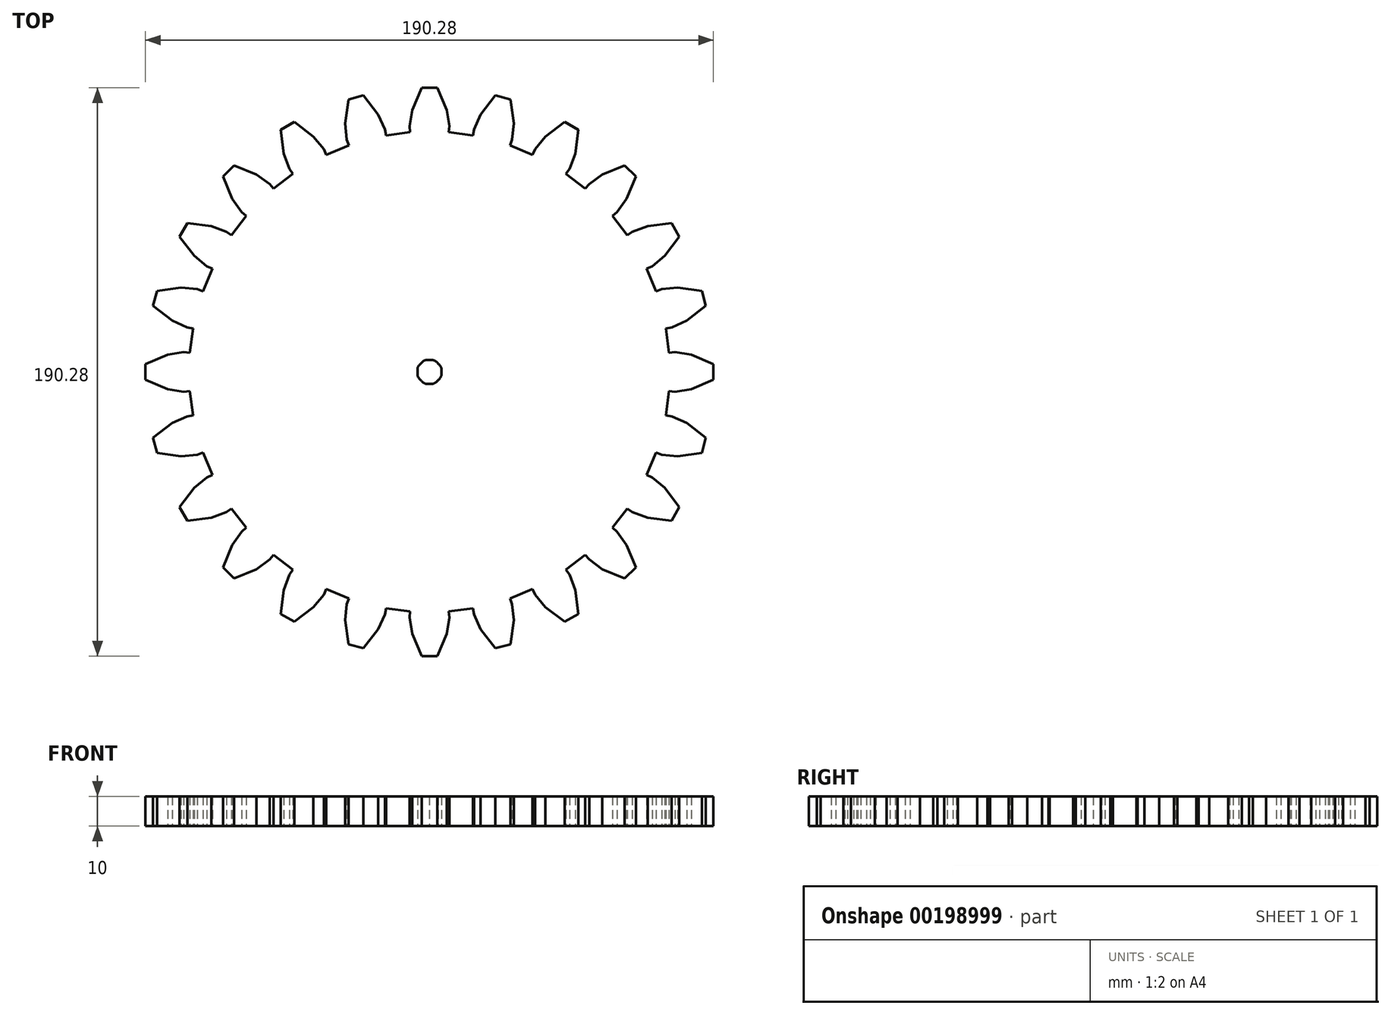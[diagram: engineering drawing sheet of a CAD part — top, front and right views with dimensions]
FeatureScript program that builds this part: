
annotation { "Feature Type Name" : "Feature", "Feature Type Description" : "" }
export const myFeature = defineFeature(function(context is Context, id is Id, definition is map)
    precondition{}
    {
        {
            var Q0;
            Q0=qCreatedBy(makeId("Top.planeOp"),FACE);
            var sketch = newSketch(context, id + "F0", { "sketchPlane" : qUnion([Q0])});
            skFitSpline(sketch, "E0", {"points": [v(4, 0) * mm, v(4, -1.06) * mm, v(3.58, -2.08) * mm, v(2.83, -2.83) * mm]});
            skFitSpline(sketch, "E1", {"points": [v(2.83, -2.83) * mm, v(2.08, -3.58) * mm, v(1.06, -4) * mm, v(0, -4) * mm]});
            skFitSpline(sketch, "E2", {"points": [v(0, -4) * mm, v(-1.06, -4) * mm, v(-2.08, -3.58) * mm, v(-2.83, -2.83) * mm]});
            skFitSpline(sketch, "E3", {"points": [v(-2.83, -2.83) * mm, v(-3.58, -2.08) * mm, v(-4, -1.06) * mm, v(-4, 0) * mm]});
            skFitSpline(sketch, "E4", {"points": [v(-4, 0) * mm, v(-4, 1.06) * mm, v(-3.58, 2.08) * mm, v(-2.83, 2.83) * mm]});
            skFitSpline(sketch, "E5", {"points": [v(-2.83, 2.83) * mm, v(-2.08, 3.58) * mm, v(-1.06, 4) * mm, v(0, 4) * mm]});
            skFitSpline(sketch, "E6", {"points": [v(0, 4) * mm, v(1.06, 4) * mm, v(2.08, 3.58) * mm, v(2.83, 2.83) * mm]});
            skFitSpline(sketch, "E7", {"points": [v(2.83, 2.83) * mm, v(3.58, 2.08) * mm, v(4, 1.06) * mm, v(4, 0) * mm]});
            skLineSegment(sketch, "E8", {"start": v(80.27, 6.46) * mm, "end": v(82.29, 6.63) * mm});
            skLineSegment(sketch, "E9", {"start": v(82.29, 6.63) * mm, "end": v(87.67, 5.75) * mm});
            skLineSegment(sketch, "E10", {"start": v(87.67, 5.75) * mm, "end": v(95.14, 2.62) * mm});
            skLineSegment(sketch, "E11", {"start": v(95.14, 2.62) * mm, "end": v(95.14, -2.62) * mm});
            skLineSegment(sketch, "E12", {"start": v(95.14, -2.62) * mm, "end": v(87.67, -5.75) * mm});
            skLineSegment(sketch, "E13", {"start": v(87.67, -5.75) * mm, "end": v(82.29, -6.63) * mm});
            skLineSegment(sketch, "E14", {"start": v(82.29, -6.63) * mm, "end": v(80.27, -6.46) * mm});
            skLineSegment(sketch, "E15", {"start": v(80.27, -6.46) * mm, "end": v(79.21, -14.53) * mm});
            skLineSegment(sketch, "E16", {"start": v(79.21, -14.53) * mm, "end": v(81.2, -14.9) * mm});
            skLineSegment(sketch, "E17", {"start": v(81.2, -14.9) * mm, "end": v(86.17, -17.14) * mm});
            skLineSegment(sketch, "E18", {"start": v(86.17, -17.14) * mm, "end": v(92.57, -22.1) * mm});
            skLineSegment(sketch, "E19", {"start": v(92.57, -22.1) * mm, "end": v(91.22, -27.15) * mm});
            skLineSegment(sketch, "E20", {"start": v(91.22, -27.15) * mm, "end": v(83.2, -28.24) * mm});
            skLineSegment(sketch, "E21", {"start": v(83.2, -28.24) * mm, "end": v(77.77, -27.7) * mm});
            skLineSegment(sketch, "E22", {"start": v(77.77, -27.7) * mm, "end": v(75.86, -27.02) * mm});
            skLineSegment(sketch, "E23", {"start": v(75.86, -27.02) * mm, "end": v(72.75, -34.54) * mm});
            skLineSegment(sketch, "E24", {"start": v(72.75, -34.54) * mm, "end": v(74.58, -35.4) * mm});
            skLineSegment(sketch, "E25", {"start": v(74.58, -35.4) * mm, "end": v(78.8, -38.86) * mm});
            skLineSegment(sketch, "E26", {"start": v(78.8, -38.86) * mm, "end": v(83.7, -45.3) * mm});
            skLineSegment(sketch, "E27", {"start": v(83.7, -45.3) * mm, "end": v(81.08, -49.84) * mm});
            skLineSegment(sketch, "E28", {"start": v(81.08, -49.84) * mm, "end": v(73.05, -48.8) * mm});
            skLineSegment(sketch, "E29", {"start": v(73.05, -48.8) * mm, "end": v(67.95, -46.88) * mm});
            skLineSegment(sketch, "E30", {"start": v(67.95, -46.88) * mm, "end": v(66.29, -45.73) * mm});
            skLineSegment(sketch, "E31", {"start": v(66.29, -45.73) * mm, "end": v(61.33, -52.2) * mm});
            skLineSegment(sketch, "E32", {"start": v(61.33, -52.2) * mm, "end": v(62.87, -53.5) * mm});
            skLineSegment(sketch, "E33", {"start": v(62.87, -53.5) * mm, "end": v(66.05, -57.93) * mm});
            skLineSegment(sketch, "E34", {"start": v(66.05, -57.93) * mm, "end": v(69.13, -65.42) * mm});
            skLineSegment(sketch, "E35", {"start": v(69.13, -65.42) * mm, "end": v(65.42, -69.13) * mm});
            skLineSegment(sketch, "E36", {"start": v(65.42, -69.13) * mm, "end": v(57.93, -66.05) * mm});
            skLineSegment(sketch, "E37", {"start": v(57.93, -66.05) * mm, "end": v(53.5, -62.87) * mm});
            skLineSegment(sketch, "E38", {"start": v(53.5, -62.87) * mm, "end": v(52.2, -61.33) * mm});
            skLineSegment(sketch, "E39", {"start": v(52.2, -61.33) * mm, "end": v(45.73, -66.29) * mm});
            skLineSegment(sketch, "E40", {"start": v(45.73, -66.29) * mm, "end": v(46.88, -67.95) * mm});
            skLineSegment(sketch, "E41", {"start": v(46.88, -67.95) * mm, "end": v(48.8, -73.05) * mm});
            skLineSegment(sketch, "E42", {"start": v(48.8, -73.05) * mm, "end": v(49.84, -81.08) * mm});
            skLineSegment(sketch, "E43", {"start": v(49.84, -81.08) * mm, "end": v(45.3, -83.7) * mm});
            skLineSegment(sketch, "E44", {"start": v(45.3, -83.7) * mm, "end": v(38.86, -78.8) * mm});
            skLineSegment(sketch, "E45", {"start": v(38.86, -78.8) * mm, "end": v(35.4, -74.58) * mm});
            skLineSegment(sketch, "E46", {"start": v(35.4, -74.58) * mm, "end": v(34.54, -72.75) * mm});
            skLineSegment(sketch, "E47", {"start": v(34.54, -72.75) * mm, "end": v(27.02, -75.86) * mm});
            skLineSegment(sketch, "E48", {"start": v(27.02, -75.86) * mm, "end": v(27.7, -77.77) * mm});
            skLineSegment(sketch, "E49", {"start": v(27.7, -77.77) * mm, "end": v(28.24, -83.2) * mm});
            skLineSegment(sketch, "E50", {"start": v(28.24, -83.2) * mm, "end": v(27.15, -91.22) * mm});
            skLineSegment(sketch, "E51", {"start": v(27.15, -91.22) * mm, "end": v(22.1, -92.57) * mm});
            skLineSegment(sketch, "E52", {"start": v(22.1, -92.57) * mm, "end": v(17.14, -86.17) * mm});
            skLineSegment(sketch, "E53", {"start": v(17.14, -86.17) * mm, "end": v(14.9, -81.2) * mm});
            skLineSegment(sketch, "E54", {"start": v(14.9, -81.2) * mm, "end": v(14.53, -79.21) * mm});
            skLineSegment(sketch, "E55", {"start": v(14.53, -79.21) * mm, "end": v(6.46, -80.27) * mm});
            skLineSegment(sketch, "E56", {"start": v(6.46, -80.27) * mm, "end": v(6.63, -82.29) * mm});
            skLineSegment(sketch, "E57", {"start": v(6.63, -82.29) * mm, "end": v(5.75, -87.67) * mm});
            skLineSegment(sketch, "E58", {"start": v(5.75, -87.67) * mm, "end": v(2.62, -95.14) * mm});
            skLineSegment(sketch, "E59", {"start": v(2.62, -95.14) * mm, "end": v(-2.62, -95.14) * mm});
            skLineSegment(sketch, "E60", {"start": v(-2.62, -95.14) * mm, "end": v(-5.75, -87.67) * mm});
            skLineSegment(sketch, "E61", {"start": v(-5.75, -87.67) * mm, "end": v(-6.63, -82.29) * mm});
            skLineSegment(sketch, "E62", {"start": v(-6.63, -82.29) * mm, "end": v(-6.46, -80.27) * mm});
            skLineSegment(sketch, "E63", {"start": v(-6.46, -80.27) * mm, "end": v(-14.53, -79.21) * mm});
            skLineSegment(sketch, "E64", {"start": v(-14.53, -79.21) * mm, "end": v(-14.9, -81.2) * mm});
            skLineSegment(sketch, "E65", {"start": v(-14.9, -81.2) * mm, "end": v(-17.14, -86.17) * mm});
            skLineSegment(sketch, "E66", {"start": v(-17.14, -86.17) * mm, "end": v(-22.1, -92.57) * mm});
            skLineSegment(sketch, "E67", {"start": v(-22.1, -92.57) * mm, "end": v(-27.15, -91.22) * mm});
            skLineSegment(sketch, "E68", {"start": v(-27.15, -91.22) * mm, "end": v(-28.24, -83.2) * mm});
            skLineSegment(sketch, "E69", {"start": v(-28.24, -83.2) * mm, "end": v(-27.7, -77.77) * mm});
            skLineSegment(sketch, "E70", {"start": v(-27.7, -77.77) * mm, "end": v(-27.02, -75.86) * mm});
            skLineSegment(sketch, "E71", {"start": v(-27.02, -75.86) * mm, "end": v(-34.54, -72.75) * mm});
            skLineSegment(sketch, "E72", {"start": v(-34.54, -72.75) * mm, "end": v(-35.4, -74.58) * mm});
            skLineSegment(sketch, "E73", {"start": v(-35.4, -74.58) * mm, "end": v(-38.86, -78.8) * mm});
            skLineSegment(sketch, "E74", {"start": v(-38.86, -78.8) * mm, "end": v(-45.3, -83.7) * mm});
            skLineSegment(sketch, "E75", {"start": v(-45.3, -83.7) * mm, "end": v(-49.84, -81.08) * mm});
            skLineSegment(sketch, "E76", {"start": v(-49.84, -81.08) * mm, "end": v(-48.8, -73.05) * mm});
            skLineSegment(sketch, "E77", {"start": v(-48.8, -73.05) * mm, "end": v(-46.88, -67.95) * mm});
            skLineSegment(sketch, "E78", {"start": v(-46.88, -67.95) * mm, "end": v(-45.73, -66.29) * mm});
            skLineSegment(sketch, "E79", {"start": v(-45.73, -66.29) * mm, "end": v(-52.2, -61.33) * mm});
            skLineSegment(sketch, "E80", {"start": v(-52.2, -61.33) * mm, "end": v(-53.5, -62.87) * mm});
            skLineSegment(sketch, "E81", {"start": v(-53.5, -62.87) * mm, "end": v(-57.93, -66.05) * mm});
            skLineSegment(sketch, "E82", {"start": v(-57.93, -66.05) * mm, "end": v(-65.42, -69.13) * mm});
            skLineSegment(sketch, "E83", {"start": v(-65.42, -69.13) * mm, "end": v(-69.13, -65.42) * mm});
            skLineSegment(sketch, "E84", {"start": v(-69.13, -65.42) * mm, "end": v(-66.05, -57.93) * mm});
            skLineSegment(sketch, "E85", {"start": v(-66.05, -57.93) * mm, "end": v(-62.87, -53.5) * mm});
            skLineSegment(sketch, "E86", {"start": v(-62.87, -53.5) * mm, "end": v(-61.33, -52.2) * mm});
            skLineSegment(sketch, "E87", {"start": v(-61.33, -52.2) * mm, "end": v(-66.29, -45.73) * mm});
            skLineSegment(sketch, "E88", {"start": v(-66.29, -45.73) * mm, "end": v(-67.95, -46.88) * mm});
            skLineSegment(sketch, "E89", {"start": v(-67.95, -46.88) * mm, "end": v(-73.05, -48.8) * mm});
            skLineSegment(sketch, "E90", {"start": v(-73.05, -48.8) * mm, "end": v(-81.08, -49.84) * mm});
            skLineSegment(sketch, "E91", {"start": v(-81.08, -49.84) * mm, "end": v(-83.7, -45.3) * mm});
            skLineSegment(sketch, "E92", {"start": v(-83.7, -45.3) * mm, "end": v(-78.8, -38.86) * mm});
            skLineSegment(sketch, "E93", {"start": v(-78.8, -38.86) * mm, "end": v(-74.58, -35.4) * mm});
            skLineSegment(sketch, "E94", {"start": v(-74.58, -35.4) * mm, "end": v(-72.75, -34.54) * mm});
            skLineSegment(sketch, "E95", {"start": v(-72.75, -34.54) * mm, "end": v(-75.86, -27.02) * mm});
            skLineSegment(sketch, "E96", {"start": v(-75.86, -27.02) * mm, "end": v(-77.77, -27.7) * mm});
            skLineSegment(sketch, "E97", {"start": v(-77.77, -27.7) * mm, "end": v(-83.2, -28.24) * mm});
            skLineSegment(sketch, "E98", {"start": v(-83.2, -28.24) * mm, "end": v(-91.22, -27.15) * mm});
            skLineSegment(sketch, "E99", {"start": v(-91.22, -27.15) * mm, "end": v(-92.57, -22.1) * mm});
            skLineSegment(sketch, "E100", {"start": v(-92.57, -22.1) * mm, "end": v(-86.17, -17.14) * mm});
            skLineSegment(sketch, "E101", {"start": v(-86.17, -17.14) * mm, "end": v(-81.2, -14.9) * mm});
            skLineSegment(sketch, "E102", {"start": v(-81.2, -14.9) * mm, "end": v(-79.21, -14.53) * mm});
            skLineSegment(sketch, "E103", {"start": v(-79.21, -14.53) * mm, "end": v(-80.27, -6.46) * mm});
            skLineSegment(sketch, "E104", {"start": v(-80.27, -6.46) * mm, "end": v(-82.29, -6.63) * mm});
            skLineSegment(sketch, "E105", {"start": v(-82.29, -6.63) * mm, "end": v(-87.67, -5.75) * mm});
            skLineSegment(sketch, "E106", {"start": v(-87.67, -5.75) * mm, "end": v(-95.14, -2.62) * mm});
            skLineSegment(sketch, "E107", {"start": v(-95.14, -2.62) * mm, "end": v(-95.14, 2.62) * mm});
            skLineSegment(sketch, "E108", {"start": v(-95.14, 2.62) * mm, "end": v(-87.67, 5.75) * mm});
            skLineSegment(sketch, "E109", {"start": v(-87.67, 5.75) * mm, "end": v(-82.29, 6.63) * mm});
            skLineSegment(sketch, "E110", {"start": v(-82.29, 6.63) * mm, "end": v(-80.27, 6.46) * mm});
            skLineSegment(sketch, "E111", {"start": v(-80.27, 6.46) * mm, "end": v(-79.21, 14.53) * mm});
            skLineSegment(sketch, "E112", {"start": v(-79.21, 14.53) * mm, "end": v(-81.2, 14.9) * mm});
            skLineSegment(sketch, "E113", {"start": v(-81.2, 14.9) * mm, "end": v(-86.17, 17.14) * mm});
            skLineSegment(sketch, "E114", {"start": v(-86.17, 17.14) * mm, "end": v(-92.57, 22.1) * mm});
            skLineSegment(sketch, "E115", {"start": v(-92.57, 22.1) * mm, "end": v(-91.22, 27.15) * mm});
            skLineSegment(sketch, "E116", {"start": v(-91.22, 27.15) * mm, "end": v(-83.2, 28.24) * mm});
            skLineSegment(sketch, "E117", {"start": v(-83.2, 28.24) * mm, "end": v(-77.77, 27.7) * mm});
            skLineSegment(sketch, "E118", {"start": v(-77.77, 27.7) * mm, "end": v(-75.86, 27.02) * mm});
            skLineSegment(sketch, "E119", {"start": v(-75.86, 27.02) * mm, "end": v(-72.75, 34.54) * mm});
            skLineSegment(sketch, "E120", {"start": v(-72.75, 34.54) * mm, "end": v(-74.58, 35.4) * mm});
            skLineSegment(sketch, "E121", {"start": v(-74.58, 35.4) * mm, "end": v(-78.8, 38.86) * mm});
            skLineSegment(sketch, "E122", {"start": v(-78.8, 38.86) * mm, "end": v(-83.7, 45.3) * mm});
            skLineSegment(sketch, "E123", {"start": v(-83.7, 45.3) * mm, "end": v(-81.08, 49.84) * mm});
            skLineSegment(sketch, "E124", {"start": v(-81.08, 49.84) * mm, "end": v(-73.05, 48.8) * mm});
            skLineSegment(sketch, "E125", {"start": v(-73.05, 48.8) * mm, "end": v(-67.95, 46.88) * mm});
            skLineSegment(sketch, "E126", {"start": v(-67.95, 46.88) * mm, "end": v(-66.29, 45.73) * mm});
            skLineSegment(sketch, "E127", {"start": v(-66.29, 45.73) * mm, "end": v(-61.33, 52.2) * mm});
            skLineSegment(sketch, "E128", {"start": v(-61.33, 52.2) * mm, "end": v(-62.87, 53.5) * mm});
            skLineSegment(sketch, "E129", {"start": v(-62.87, 53.5) * mm, "end": v(-66.05, 57.93) * mm});
            skLineSegment(sketch, "E130", {"start": v(-66.05, 57.93) * mm, "end": v(-69.13, 65.42) * mm});
            skLineSegment(sketch, "E131", {"start": v(-69.13, 65.42) * mm, "end": v(-65.42, 69.13) * mm});
            skLineSegment(sketch, "E132", {"start": v(-65.42, 69.13) * mm, "end": v(-57.93, 66.05) * mm});
            skLineSegment(sketch, "E133", {"start": v(-57.93, 66.05) * mm, "end": v(-53.5, 62.87) * mm});
            skLineSegment(sketch, "E134", {"start": v(-53.5, 62.87) * mm, "end": v(-52.2, 61.33) * mm});
            skLineSegment(sketch, "E135", {"start": v(-52.2, 61.33) * mm, "end": v(-45.73, 66.29) * mm});
            skLineSegment(sketch, "E136", {"start": v(-45.73, 66.29) * mm, "end": v(-46.88, 67.95) * mm});
            skLineSegment(sketch, "E137", {"start": v(-46.88, 67.95) * mm, "end": v(-48.8, 73.05) * mm});
            skLineSegment(sketch, "E138", {"start": v(-48.8, 73.05) * mm, "end": v(-49.84, 81.08) * mm});
            skLineSegment(sketch, "E139", {"start": v(-49.84, 81.08) * mm, "end": v(-45.3, 83.7) * mm});
            skLineSegment(sketch, "E140", {"start": v(-45.3, 83.7) * mm, "end": v(-38.86, 78.8) * mm});
            skLineSegment(sketch, "E141", {"start": v(-38.86, 78.8) * mm, "end": v(-35.4, 74.58) * mm});
            skLineSegment(sketch, "E142", {"start": v(-35.4, 74.58) * mm, "end": v(-34.54, 72.75) * mm});
            skLineSegment(sketch, "E143", {"start": v(-34.54, 72.75) * mm, "end": v(-27.02, 75.86) * mm});
            skLineSegment(sketch, "E144", {"start": v(-27.02, 75.86) * mm, "end": v(-27.7, 77.77) * mm});
            skLineSegment(sketch, "E145", {"start": v(-27.7, 77.77) * mm, "end": v(-28.24, 83.2) * mm});
            skLineSegment(sketch, "E146", {"start": v(-28.24, 83.2) * mm, "end": v(-27.15, 91.22) * mm});
            skLineSegment(sketch, "E147", {"start": v(-27.15, 91.22) * mm, "end": v(-22.1, 92.57) * mm});
            skLineSegment(sketch, "E148", {"start": v(-22.1, 92.57) * mm, "end": v(-17.14, 86.17) * mm});
            skLineSegment(sketch, "E149", {"start": v(-17.14, 86.17) * mm, "end": v(-14.9, 81.2) * mm});
            skLineSegment(sketch, "E150", {"start": v(-14.9, 81.2) * mm, "end": v(-14.53, 79.21) * mm});
            skLineSegment(sketch, "E151", {"start": v(-14.53, 79.21) * mm, "end": v(-6.46, 80.27) * mm});
            skLineSegment(sketch, "E152", {"start": v(-6.46, 80.27) * mm, "end": v(-6.63, 82.29) * mm});
            skLineSegment(sketch, "E153", {"start": v(-6.63, 82.29) * mm, "end": v(-5.75, 87.67) * mm});
            skLineSegment(sketch, "E154", {"start": v(-5.75, 87.67) * mm, "end": v(-2.62, 95.14) * mm});
            skLineSegment(sketch, "E155", {"start": v(-2.62, 95.14) * mm, "end": v(2.62, 95.14) * mm});
            skLineSegment(sketch, "E156", {"start": v(2.62, 95.14) * mm, "end": v(5.75, 87.67) * mm});
            skLineSegment(sketch, "E157", {"start": v(5.75, 87.67) * mm, "end": v(6.63, 82.29) * mm});
            skLineSegment(sketch, "E158", {"start": v(6.63, 82.29) * mm, "end": v(6.46, 80.27) * mm});
            skLineSegment(sketch, "E159", {"start": v(6.46, 80.27) * mm, "end": v(14.53, 79.21) * mm});
            skLineSegment(sketch, "E160", {"start": v(14.53, 79.21) * mm, "end": v(14.9, 81.2) * mm});
            skLineSegment(sketch, "E161", {"start": v(14.9, 81.2) * mm, "end": v(17.14, 86.17) * mm});
            skLineSegment(sketch, "E162", {"start": v(17.14, 86.17) * mm, "end": v(22.1, 92.57) * mm});
            skLineSegment(sketch, "E163", {"start": v(22.1, 92.57) * mm, "end": v(27.15, 91.22) * mm});
            skLineSegment(sketch, "E164", {"start": v(27.15, 91.22) * mm, "end": v(28.24, 83.2) * mm});
            skLineSegment(sketch, "E165", {"start": v(28.24, 83.2) * mm, "end": v(27.7, 77.77) * mm});
            skLineSegment(sketch, "E166", {"start": v(27.7, 77.77) * mm, "end": v(27.02, 75.86) * mm});
            skLineSegment(sketch, "E167", {"start": v(27.02, 75.86) * mm, "end": v(34.54, 72.75) * mm});
            skLineSegment(sketch, "E168", {"start": v(34.54, 72.75) * mm, "end": v(35.4, 74.58) * mm});
            skLineSegment(sketch, "E169", {"start": v(35.4, 74.58) * mm, "end": v(38.86, 78.8) * mm});
            skLineSegment(sketch, "E170", {"start": v(38.86, 78.8) * mm, "end": v(45.3, 83.7) * mm});
            skLineSegment(sketch, "E171", {"start": v(45.3, 83.7) * mm, "end": v(49.84, 81.08) * mm});
            skLineSegment(sketch, "E172", {"start": v(49.84, 81.08) * mm, "end": v(48.8, 73.05) * mm});
            skLineSegment(sketch, "E173", {"start": v(48.8, 73.05) * mm, "end": v(46.88, 67.95) * mm});
            skLineSegment(sketch, "E174", {"start": v(46.88, 67.95) * mm, "end": v(45.73, 66.29) * mm});
            skLineSegment(sketch, "E175", {"start": v(45.73, 66.29) * mm, "end": v(52.2, 61.33) * mm});
            skLineSegment(sketch, "E176", {"start": v(52.2, 61.33) * mm, "end": v(53.5, 62.87) * mm});
            skLineSegment(sketch, "E177", {"start": v(53.5, 62.87) * mm, "end": v(57.93, 66.05) * mm});
            skLineSegment(sketch, "E178", {"start": v(57.93, 66.05) * mm, "end": v(65.42, 69.13) * mm});
            skLineSegment(sketch, "E179", {"start": v(65.42, 69.13) * mm, "end": v(69.13, 65.42) * mm});
            skLineSegment(sketch, "E180", {"start": v(69.13, 65.42) * mm, "end": v(66.05, 57.93) * mm});
            skLineSegment(sketch, "E181", {"start": v(66.05, 57.93) * mm, "end": v(62.87, 53.5) * mm});
            skLineSegment(sketch, "E182", {"start": v(62.87, 53.5) * mm, "end": v(61.33, 52.2) * mm});
            skLineSegment(sketch, "E183", {"start": v(61.33, 52.2) * mm, "end": v(66.29, 45.73) * mm});
            skLineSegment(sketch, "E184", {"start": v(66.29, 45.73) * mm, "end": v(67.95, 46.88) * mm});
            skLineSegment(sketch, "E185", {"start": v(67.95, 46.88) * mm, "end": v(73.05, 48.8) * mm});
            skLineSegment(sketch, "E186", {"start": v(73.05, 48.8) * mm, "end": v(81.08, 49.84) * mm});
            skLineSegment(sketch, "E187", {"start": v(81.08, 49.84) * mm, "end": v(83.7, 45.3) * mm});
            skLineSegment(sketch, "E188", {"start": v(83.7, 45.3) * mm, "end": v(78.8, 38.86) * mm});
            skLineSegment(sketch, "E189", {"start": v(78.8, 38.86) * mm, "end": v(74.58, 35.4) * mm});
            skLineSegment(sketch, "E190", {"start": v(74.58, 35.4) * mm, "end": v(72.75, 34.54) * mm});
            skLineSegment(sketch, "E191", {"start": v(72.75, 34.54) * mm, "end": v(75.86, 27.02) * mm});
            skLineSegment(sketch, "E192", {"start": v(75.86, 27.02) * mm, "end": v(77.77, 27.7) * mm});
            skLineSegment(sketch, "E193", {"start": v(77.77, 27.7) * mm, "end": v(83.2, 28.24) * mm});
            skLineSegment(sketch, "E194", {"start": v(83.2, 28.24) * mm, "end": v(91.22, 27.15) * mm});
            skLineSegment(sketch, "E195", {"start": v(91.22, 27.15) * mm, "end": v(92.57, 22.1) * mm});
            skLineSegment(sketch, "E196", {"start": v(92.57, 22.1) * mm, "end": v(86.17, 17.14) * mm});
            skLineSegment(sketch, "E197", {"start": v(86.17, 17.14) * mm, "end": v(81.2, 14.9) * mm});
            skLineSegment(sketch, "E198", {"start": v(81.2, 14.9) * mm, "end": v(79.21, 14.53) * mm});
            skLineSegment(sketch, "E199", {"start": v(79.21, 14.53) * mm, "end": v(80.27, 6.46) * mm});
            skSolve(sketch);
        }
        {
            var Q0;
            Q0 = qSketchRegion(id + "F0", true);
            extrude(context, id + "F1", {"entities" : qUnion([Q0]), "depth" : 10 * mm});
        }
    });
